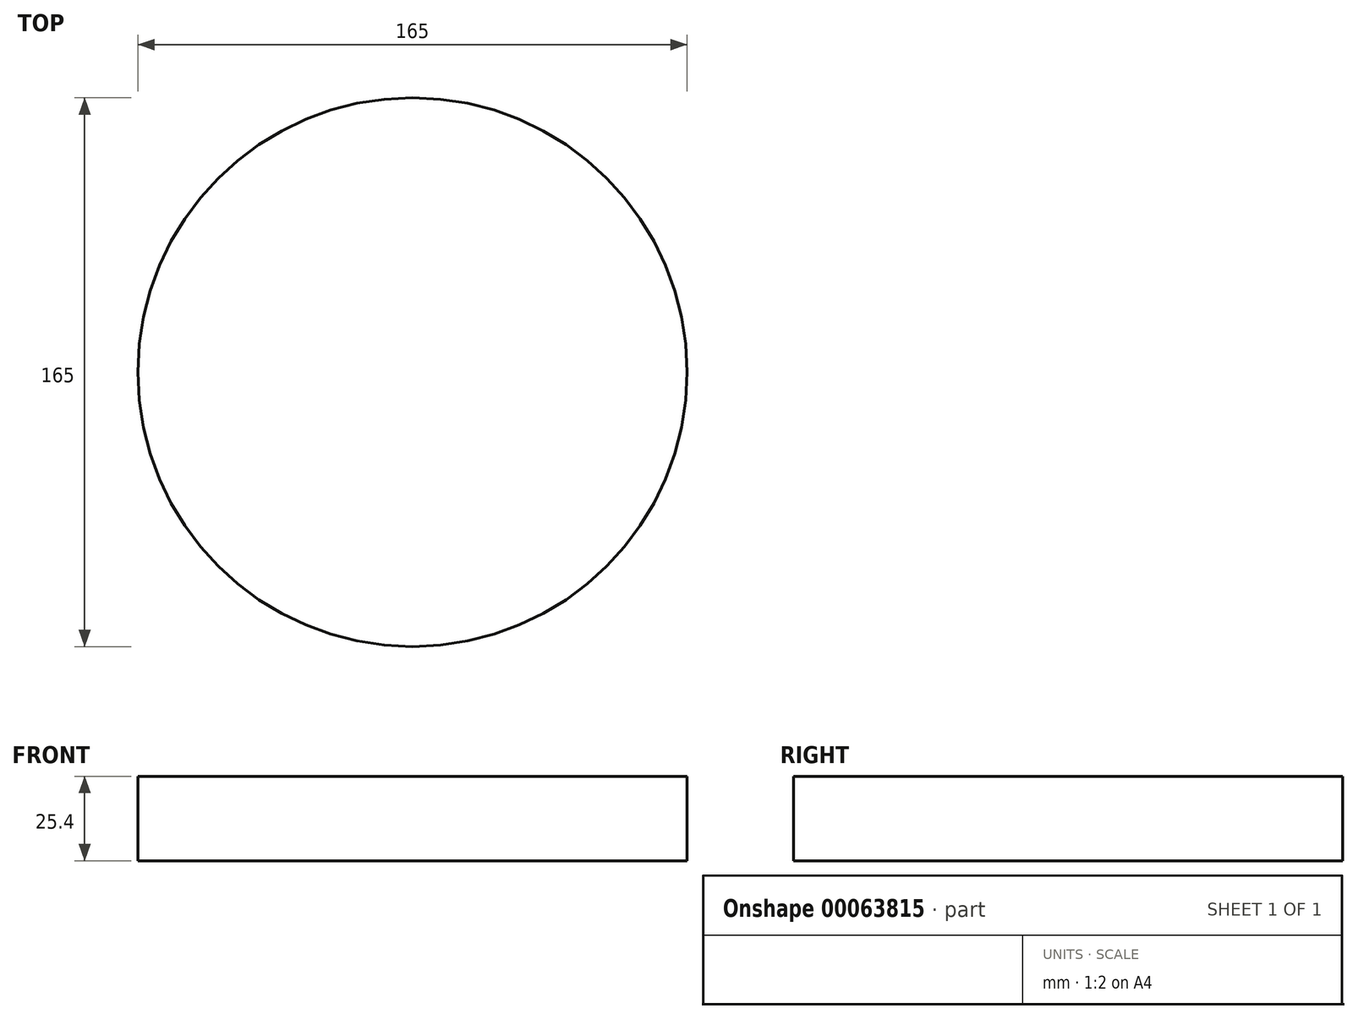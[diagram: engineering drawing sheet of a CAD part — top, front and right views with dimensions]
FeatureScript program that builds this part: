
annotation { "Feature Type Name" : "Feature", "Feature Type Description" : "" }
export const myFeature = defineFeature(function(context is Context, id is Id, definition is map)
    precondition{}
    {
        {
            var Q0;
            Q0=qCreatedBy(makeId("Top.planeOp"),FACE);
            var sketch = newSketch(context, id + "F0", { "sketchPlane" : qUnion([Q0])});
            skCircle(sketch, "E0", {"center": v(0, 0) * mm, "radius": 82.5 * mm});
            skSolve(sketch);
        }
        {
            var Q0;
            Q0=makeQuery(id+"F0.imprint","IMPRINT",FACE,{"disambiguationData":[TD([[makeQuery(id+"F0.imprint","IMPRINT",EDGE,{"derivedFrom":sQuery(id+"F0.wireOp",EDGE,"E0")}),1.0]])]});
            extrude(context, id + "F1", {"entities" : qUnion([Q0]), "depth" : 25.4 * mm});
        }
    });
